# Revit family: Montageschiene 35- 21-2,0 fbv 6m
name_source: partatom
category: HLS-Bauteile
revit_build: Autodesk Revit 2017 (Build: 20190507_1515(x64)
units: mm (PartAtom-declared; Revit-internal decimal feet)

## family parameters
Arbeitsebenenbasiert = Ja
Beim Laden mit Abzugskörper schneiden = Nein
Bemaßung runder Anschluss = Durchmesser verwenden
Gemeinsam genutzt = Ja
Immer vertikal = Nein
Raumberechnungspunkt = Nein
Teiletyp = Normal

## types (1)
- Profil  35- 21-2,0 fbv L=6000
    Abmessung = 35/21/2.0 mm
    Artikelnummer = 0800026
    Breite = 35 mm  [stored 0.114829 ft]
    Bund = 576 m
    EAN = 4250928419163
    Fabrikat = MEFA
    Firma = MEFA Befestigungs- und Montagesysteme GmbH
    Fläche (schwächster Profilquerschnitt) = 0 m²
    Gewicht = 1,16 kg
    Höhe = 21 mm
    Kurztext1 = Montageschiene C-Profil
    Kurztext2 = 35 / 21 / 2 mm L= 6 m fbv
    Langloch = 10.5 x 38.5 mm
    Länge = 6000 mm  [stored 19.685 ft]
    Material = Stahl
    Materialname = S250
    Mengeneinheit = m
    Oberflaeche = feuerbandverzinkt
    Schlitzbreite = 18 mm
    Schwerpunktabstand eo = 0,96 cm
    Schwerpunktabstand eu = 1,14 cm
    Schwerpunktabstand ez = 1,75 cm
    Streckgrenze = 250 N/mm²
    Stärke = 2 mm  [stored 0.00656168 ft]
    Torsionswiderstandsmoment Wt = cm³
    Trägheitsradius iy = 0,76 cm
    Trägheitsradius iz = 1,42 cm
    Vorgabe-Ansicht = 1219 mm
    Widerstandsmoment Wy = 0,71 cm³
    Widerstandsmoment Wz = 1,61 cm³
    vpe = 48 m

note: [stored X ft] marks values corroborated as IEEE doubles in the binary element streams (Revit-internal decimal feet)
